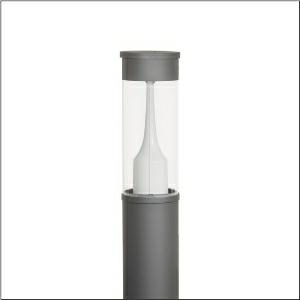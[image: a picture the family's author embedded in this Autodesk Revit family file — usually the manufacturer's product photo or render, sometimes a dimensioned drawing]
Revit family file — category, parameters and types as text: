
# Revit family: city-light_260_iq___st1_2a_5xa5295ef14h_2f06
name_source: partatom
category: Lighting Fixtures
units: mm (PartAtom-declared; Revit-internal decimal feet)

## family parameters
Cut with Voids When Loaded = No
Host = Face
Light Source = No
Part Type = Normal
Room Calculation Point = No
Round Connector Dimension = Use Diameter
Shared = No

## types (1)
- --- (1 x LED, 1540 lm, 10.5 W, 3000K)
    Apparent Load = 11 VA
    CIE Flux Codes = 22 61 93 96 100
    Color Rendering = 70
    Color Temperature = 3000K
    Default Elevation = 1800 mm
    Description = City-Light 260 iQ, light pillar, Module 540 iQ-SR, primary light control with 3 zone facetted reflector, of plastic, silver coated, highly specular, structured, primary optical cover: cover, of PMMA, transparent, light distribution: ST1.2a, primary light characteristic: asymmetric, LED, High Power LED, rated luminous flux: 1.540lm, luminous efficacy: 147lm/W, light colour: 730, colour temperature: 3000K, control gear: ECG iQ, control: Auto-Match, Temp-Guard, Lumen-Switch, Night-Set, Smart-Wire, Light-Fading, Desk-Remote (wireless, voltage-free reading and setting of iQ features in the workshop via application-optimized NFC function/RFID function), optimised constant luminous flux control (CLO 2.0), Street-Remote, presetting dimming logarithmic, with terminal, 6-pole, max. 2.5mm², mains connection: 220..240V, AC, 50/60Hz, start of lifetime: 11W, end of lifetime: 11W, reduction: 5W, luminaire housing, cylindrical, of extruded aluminium section, coated, Siteco® metallic grey (DB 702S), length: 2.600mm, diameter: 200mm, Module 540 iQ-SR, traffic white (RAL 9016), equipment: standard, protection rating (complete): IP65, insulation class (complete): insulation class II (safety insulation), certification: CE, ENEC, VDE, packaging unit: 1 piece

Light Distribution: ST1.2a
    Height = 500 mm
    Lamp = 1 x LED
    Lamp Light Flux = 1540 lm
    Lamp Power = 10.5 W
    Lamp count = 1
    Length = 200 mm  [stored 0.656168 ft]
    Luminous efficacy = 147 lm/W
    Manufacturer = Siteco
    ModVariant = No
    Model = 5XA5295EF14H
    Number of Poles = 1
    OnlyDefault = Yes
    Power Factor = 1
    Product Name = City-Light 260 iQ | ST1.2a
    Product group = light pillar | pylon top
    ProductGroupID = 6103
    Protection Class = Protection class II
    Protection Degree = IP 65
    RLX_Detail_Level = 1
    RlxData = <blob elided: 60657 chars, md5=2aded2f7>
    Socket = socket
    Standby Power = 0 W
    System Light Flux = 1540 lm
    System Power = 11 W
    Type Comments = factory setting: luminous flux: 100 % | dim-lin: 254 | 419 mA
    Type Image = l_1006918.jpg
    URL = http://relux.com
    VarID = @adj_070449
    Voltage = 0 V
    Weight = 0.00 kg
    Width = 0 mm  [stored 0 ft]

note: [stored X ft] marks values corroborated as IEEE doubles in the binary element streams (Revit-internal decimal feet)

## geometry (parser evidence)
native form markers: Blend x4, Sweep x11
no freeform markers — native parametric forms only
